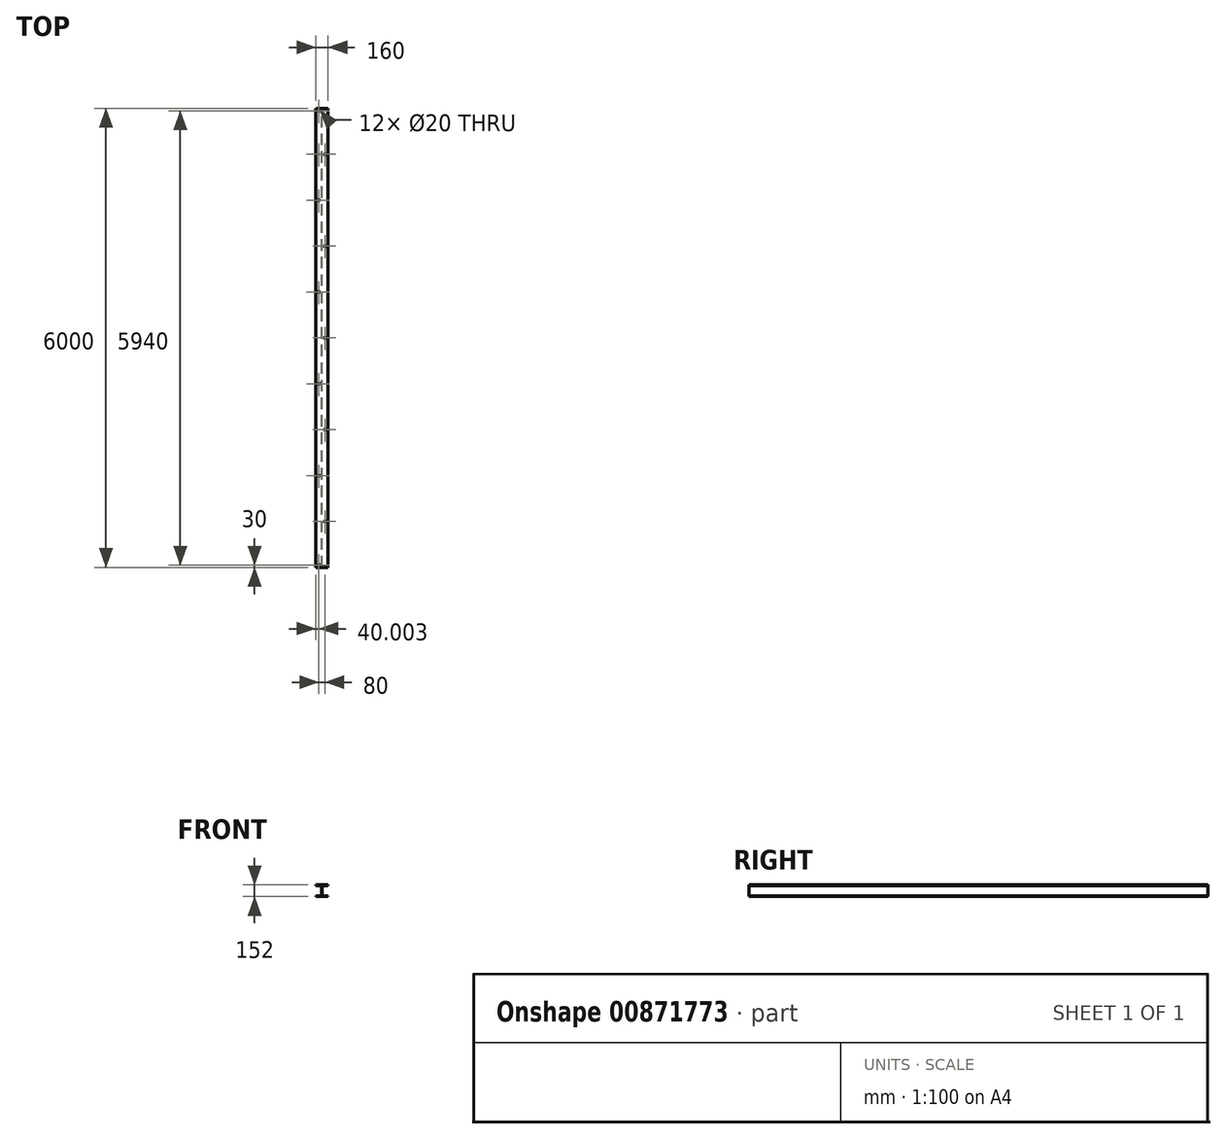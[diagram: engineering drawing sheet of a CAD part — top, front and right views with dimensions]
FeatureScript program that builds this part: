
annotation { "Feature Type Name" : "Feature", "Feature Type Description" : "" }
export const myFeature = defineFeature(function(context is Context, id is Id, definition is map)
    precondition{}
    {
        {
            var Q0;
            Q0=qCreatedBy(makeId("Front.planeOp"),FACE);
            var sketch = newSketch(context, id + "F0", { "sketchPlane" : qUnion([Q0])});
            skLineSegment(sketch, "E0.bottom", {"start": v(-85.3, -46.97) * mm, "end": v(-23.3, -46.97) * mm});
            skLineSegment(sketch, "E0.top", {"start": v(-85.3, -55.97) * mm, "end": v(74.7, -55.97) * mm});
            skLineSegment(sketch, "E0.left", {"start": v(-85.3, -46.97) * mm, "end": v(-85.3, -55.97) * mm});
            skLineSegment(sketch, "E0.right", {"start": v(74.7, -46.97) * mm, "end": v(74.7, -55.97) * mm});
            skLineSegment(sketch, "E1.bottom", {"start": v(-5.3, -46.97) * mm, "end": v(-2.3, -46.97) * mm});
            skLineSegment(sketch, "E1.top", {"start": v(-5.3, 87.03) * mm, "end": v(-2.3, 87.03) * mm});
            skLineSegment(sketch, "E1.left", {"start": v(-5.3, -46.97) * mm, "end": v(-5.3, 87.03) * mm});
            skLineSegment(sketch, "E1.right", {"start": v(-2.3, -31.97) * mm, "end": v(-2.3, 72.03) * mm});
            skLineSegment(sketch, "E2.bottom", {"start": v(-5.3, -46.97) * mm, "end": v(-8.3, -46.97) * mm});
            skLineSegment(sketch, "E2.top", {"start": v(-5.3, 87.03) * mm, "end": v(-8.3, 87.03) * mm});
            skLineSegment(sketch, "E2.right", {"start": v(-8.3, -31.97) * mm, "end": v(-8.3, 72.03) * mm});
            skLineSegment(sketch, "E3.bottom", {"start": v(-85.3, 87.03) * mm, "end": v(-23.3, 87.03) * mm});
            skLineSegment(sketch, "E3.top", {"start": v(-85.3, 96.03) * mm, "end": v(74.7, 96.03) * mm});
            skLineSegment(sketch, "E3.left", {"start": v(-85.3, 87.03) * mm, "end": v(-85.3, 96.03) * mm});
            skLineSegment(sketch, "E3.right", {"start": v(74.7, 87.03) * mm, "end": v(74.7, 96.03) * mm});
            skArc(sketch, "E4.filletArc", {"start": v(-8.3, 72.03) * mm, "mid": v(-12.7, 82.64) * mm, "end": v(-23.3, 87.03) * mm});
            skPoint(sketch, "E5.newPointA", {"position": v(74.7, -46.97) * mm});
            skArc(sketch, "E5.filletArc", {"start": v(-23.3, -46.97) * mm, "mid": v(-12.7, -42.57) * mm, "end": v(-8.3, -31.97) * mm});
            skLineSegment(sketch, "E6", {"start": v(12.7, -46.97) * mm, "end": v(74.7, -46.97) * mm});
            skLineSegment(sketch, "E7", {"start": v(12.7, 87.03) * mm, "end": v(74.7, 87.03) * mm});
            skPoint(sketch, "E8.visualSharp", {"position": v(-2.3, 87.03) * mm});
            skArc(sketch, "E8.filletArc", {"start": v(12.7, 87.03) * mm, "mid": v(2.09, 82.64) * mm, "end": v(-2.3, 72.03) * mm});
            skPoint(sketch, "E9.visualSharp", {"position": v(-2.3, -46.97) * mm});
            skArc(sketch, "E9.filletArc", {"start": v(-2.3, -31.97) * mm, "mid": v(2.09, -42.57) * mm, "end": v(12.7, -46.97) * mm});
            skSolve(sketch);
        }
        {
            var Q0;
            Q0=makeQuery(id+"F0.imprint","IMPRINT",FACE,{"disambiguationData":[TD([[makeQuery(id+"F0.imprint","IMPRINT",EDGE,{"derivedFrom":sQuery(id+"F0.wireOp",EDGE,"E0.bottom")}),-1.0]])]});
            extrude(context, id + "F1", {"entities" : qUnion([Q0]), "depth" : 6000 * mm, "offsetDistance" : 25 * mm});
        }
        {
            var Q0;
            Q0=makeQuery(id+"F1.opExtrude","SWEPT_FACE",FACE,{"disambiguationData":[OSD([sQuery(id+"F0.wireOp",EDGE,"E3.top")])]});
            var sketch = newSketch(context, id + "F2", { "sketchPlane" : qUnion([Q0])});
            skLineSegment(sketch, "E10.0.0", {"start": v(74.7, 0) * mm, "end": v(-85.3, 0) * mm});
            skLineSegment(sketch, "E10.0.1", {"start": v(-85.3, 0) * mm, "end": v(-85.3, -6000) * mm});
            skLineSegment(sketch, "E10.0.2", {"start": v(-85.3, -6000) * mm, "end": v(74.7, -6000) * mm});
            skLineSegment(sketch, "E10.0.3", {"start": v(74.7, -6000) * mm, "end": v(74.7, 0) * mm});
            skCircle(sketch, "E11", {"center": v(-45.3, -30) * mm, "radius": 10 * mm});
            skCircle(sketch, "E12", {"center": v(34.7, -600) * mm, "radius": 10 * mm});
            skCircle(sketch, "E13", {"center": v(-45.3, -1200) * mm, "radius": 10 * mm});
            skCircle(sketch, "E14", {"center": v(34.7, -1800) * mm, "radius": 10 * mm});
            skCircle(sketch, "E15.0.1.0", {"center": v(-45.3, -2400) * mm, "radius": 10 * mm});
            skCircle(sketch, "E15.0.1.1", {"center": v(34.7, -3000) * mm, "radius": 10 * mm});
            skCircle(sketch, "E15.0.2.0", {"center": v(-45.3, -3600) * mm, "radius": 10 * mm});
            skCircle(sketch, "E15.0.2.1", {"center": v(34.7, -4200) * mm, "radius": 10 * mm});
            skCircle(sketch, "E15.0.3.0", {"center": v(-45.3, -4800) * mm, "radius": 10 * mm});
            skCircle(sketch, "E15.0.3.1", {"center": v(34.7, -5400) * mm, "radius": 10 * mm});
            skCircle(sketch, "E15.0.4.1", {"center": v(34.7, -6600) * mm, "radius": 10 * mm});
            skLineSegment(sketch, "E15.direction1", {"start": v(-45.3, -1200) * mm, "end": v(-20.3, -1200) * mm, "construction": true});
            skLineSegment(sketch, "E15.direction2", {"start": v(-45.3, -1200) * mm, "end": v(-45.3, -2400) * mm, "construction": true});
            skCircle(sketch, "E16", {"center": v(-45.3, -5970) * mm, "radius": 10 * mm});
            skSolve(sketch);
        }
        {
            var Q0;
            Q0=makeQuery(id+"F2.imprint","IMPRINT",FACE,{"disambiguationData":[TD([[makeQuery(id+"F2.imprint","IMPRINT",EDGE,{"derivedFrom":sQuery(id+"F2.wireOp",EDGE,"E15.0.4.1")}),1.0]])]});
            var Q1;
            Q1=makeQuery(id+"F2.imprint","IMPRINT",FACE,{"disambiguationData":[TD([[makeQuery(id+"F2.imprint","IMPRINT",EDGE,{"derivedFrom":sQuery(id+"F2.wireOp",EDGE,"E15.0.3.1")}),1.0]])]});
            var Q2;
            Q2=makeQuery(id+"F2.imprint","IMPRINT",FACE,{"disambiguationData":[TD([[makeQuery(id+"F2.imprint","IMPRINT",EDGE,{"derivedFrom":sQuery(id+"F2.wireOp",EDGE,"E16")}),1.0]])]});
            var Q3;
            Q3=makeQuery(id+"F2.imprint","IMPRINT",FACE,{"disambiguationData":[TD([[makeQuery(id+"F2.imprint","IMPRINT",EDGE,{"derivedFrom":sQuery(id+"F2.wireOp",EDGE,"E15.0.3.0")}),1.0]])]});
            var Q4;
            Q4=makeQuery(id+"F2.imprint","IMPRINT",FACE,{"disambiguationData":[TD([[makeQuery(id+"F2.imprint","IMPRINT",EDGE,{"derivedFrom":sQuery(id+"F2.wireOp",EDGE,"E15.0.2.1")}),1.0]])]});
            var Q5;
            Q5=makeQuery(id+"F2.imprint","IMPRINT",FACE,{"disambiguationData":[TD([[makeQuery(id+"F2.imprint","IMPRINT",EDGE,{"derivedFrom":sQuery(id+"F2.wireOp",EDGE,"E15.0.2.0")}),1.0]])]});
            var Q6;
            Q6=makeQuery(id+"F2.imprint","IMPRINT",FACE,{"disambiguationData":[TD([[makeQuery(id+"F2.imprint","IMPRINT",EDGE,{"derivedFrom":sQuery(id+"F2.wireOp",EDGE,"E15.0.1.1")}),1.0]])]});
            var Q7;
            Q7=makeQuery(id+"F2.imprint","IMPRINT",FACE,{"disambiguationData":[TD([[makeQuery(id+"F2.imprint","IMPRINT",EDGE,{"derivedFrom":sQuery(id+"F2.wireOp",EDGE,"E15.0.1.0")}),1.0]])]});
            var Q8;
            Q8=makeQuery(id+"F2.imprint","IMPRINT",FACE,{"disambiguationData":[TD([[makeQuery(id+"F2.imprint","IMPRINT",EDGE,{"derivedFrom":sQuery(id+"F2.wireOp",EDGE,"E14")}),1.0]])]});
            var Q9;
            Q9=makeQuery(id+"F2.imprint","IMPRINT",FACE,{"disambiguationData":[TD([[makeQuery(id+"F2.imprint","IMPRINT",EDGE,{"derivedFrom":sQuery(id+"F2.wireOp",EDGE,"E13")}),1.0]])]});
            var Q10;
            Q10=makeQuery(id+"F2.imprint","IMPRINT",FACE,{"disambiguationData":[TD([[makeQuery(id+"F2.imprint","IMPRINT",EDGE,{"derivedFrom":sQuery(id+"F2.wireOp",EDGE,"E12")}),1.0]])]});
            var Q11;
            Q11=makeQuery(id+"F2.imprint","IMPRINT",FACE,{"disambiguationData":[TD([[makeQuery(id+"F2.imprint","IMPRINT",EDGE,{"derivedFrom":sQuery(id+"F2.wireOp",EDGE,"E11")}),1.0]])]});
            extrude(context, id + "F3", {"entities" : qUnion([Q0, Q1, Q2, Q3, Q4, Q5, Q6, Q7, Q8, Q9, Q10, Q11]), "operationType" : NewBodyOperationType.REMOVE, "oppositeDirection" : true, "depth" : 25 * mm, "offsetDistance" : 25 * mm});
        }
        {
            var Q0;
            Q0=makeQuery(id+"F1.opExtrude","SWEPT_FACE",FACE,{"disambiguationData":[OSD([sQuery(id+"F0.wireOp",EDGE,"E0.top")])]});
            var sketch = newSketch(context, id + "F4", { "sketchPlane" : qUnion([Q0])});
            skCircle(sketch, "E17", {"center": v(-45.3, 600) * mm, "radius": 10 * mm});
            skSolve(sketch);
        }
        {
            var Q0;
            Q0=makeQuery(id+"F4.imprint","IMPRINT",FACE,{"disambiguationData":[TD([[makeQuery(id+"F4.imprint","IMPRINT",EDGE,{"derivedFrom":sQuery(id+"F4.wireOp",EDGE,"E17")}),1.0]])]});
            extrude(context, id + "F5", {"entities" : qUnion([Q0]), "operationType" : NewBodyOperationType.REMOVE, "oppositeDirection" : true, "depth" : 25 * mm, "offsetDistance" : 25 * mm});
        }
    });
